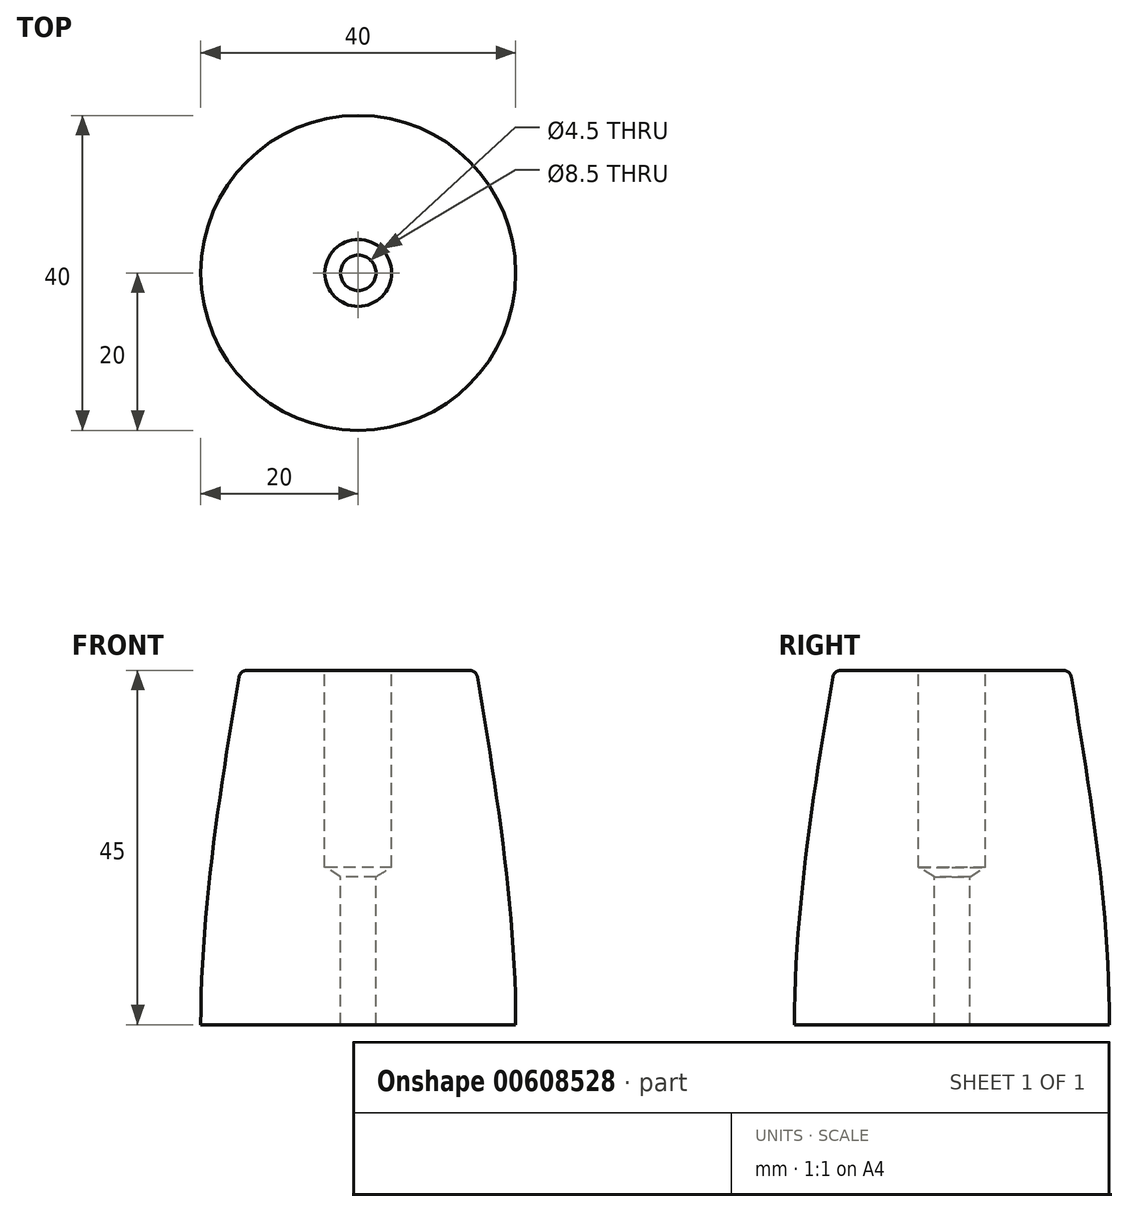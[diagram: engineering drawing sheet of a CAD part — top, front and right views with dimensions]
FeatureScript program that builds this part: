
annotation { "Feature Type Name" : "Feature", "Feature Type Description" : "" }
export const myFeature = defineFeature(function(context is Context, id is Id, definition is map)
    precondition{}
    {
        {
            var Q0;
            Q0=qCreatedBy(makeId("Top.planeOp"),FACE);
            var sketch = newSketch(context, id + "F0", { "sketchPlane" : qUnion([Q0])});
            skCircle(sketch, "E0", {"center": v(0, 0) * mm, "radius": 20 * mm});
            skSolve(sketch);
        }
        {
            var Q0;
            Q0=qCreatedBy(makeId("Top.planeOp"),FACE);
            cPlane(context, id + "F1", {"entities" : qUnion([Q0]), "cplaneType" : CPlaneType.OFFSET, "offset" : 45 * mm, "width" : 150 * mm, "height" : 150 * mm});
        }
        {
            var Q0;
            Q0=qCreatedBy(id+"F1.planeOp",FACE);
            var sketch = newSketch(context, id + "F2", { "sketchPlane" : qUnion([Q0])});
            skCircle(sketch, "E1.0", {"center": v(0, 0) * mm, "radius": 20 * mm, "construction": true});
            skCircle(sketch, "E2.0", {"center": v(0, 0) * mm, "radius": 15 * mm});
            skSolve(sketch);
        }
        {
            var Q0;
            Q0=makeQuery(id+"F0.imprint","IMPRINT",FACE,{"disambiguationData":[TD([[makeQuery(id+"F0.imprint","IMPRINT",EDGE,{"derivedFrom":sQuery(id+"F0.wireOp",EDGE,"E0")}),1.0]])]});
            var Q1;
            Q1=makeQuery(id+"F2.imprint","IMPRINT",FACE,{"disambiguationData":[TD([[makeQuery(id+"F2.imprint","IMPRINT",EDGE,{"derivedFrom":sQuery(id+"F2.wireOp",EDGE,"E2.0")}),1.0]])]});
            loft(context, id + "F3", {"startCondition" : LoftEndDerivativeType.NORMAL_TO_PROFILE, "startMagnitude" : 1, "sheetProfilesArray" : [{ "sheetProfileEntities" : qUnion([Q0]) }, { "sheetProfileEntities" : qUnion([Q1]) }]});
        }
        {
            var Q0;
            Q0=sQuery(id+"F2.wireOp",VERTEX,"E1.0.center");
            var Q1;
            Q1=makeQuery(id+"F3.opLoft","SWEPT_BODY",BODY,{"disambiguationData":[OSD([makeQuery(id+"F0.imprint","IMPRINT",FACE,{"disambiguationData":[TD([[makeQuery(id+"F0.imprint","IMPRINT",EDGE,{"derivedFrom":sQuery(id+"F0.wireOp",EDGE,"E0")}),1.0]])]}),makeQuery(id+"F2.imprint","IMPRINT",FACE,{"disambiguationData":[TD([[makeQuery(id+"F2.imprint","IMPRINT",EDGE,{"derivedFrom":sQuery(id+"F2.wireOp",EDGE,"E2.0")}),1.0]])]})])]});
            hole(context, id + "F4", {"style" : HoleStyle.SIMPLE, "endStyle" : HoleEndStyle.THROUGH, "holeDiameter" : 4.5 * mm, "majorDiameter" : 5 * mm, "isTappedThrough" : true, "tappedDepth" : 12 * mm, "tapClearance" : 3, "locations" : qUnion([Q0]), "scope" : qUnion([Q1])});
        }
        {
            var Q0;
            Q0=sQuery(id+"F2.wireOp",VERTEX,"E1.0.center");
            var Q1;
            Q1=makeQuery(id+"F3.opLoft","SWEPT_BODY",BODY,{"disambiguationData":[OSD([makeQuery(id+"F0.imprint","IMPRINT",FACE,{"disambiguationData":[TD([[makeQuery(id+"F0.imprint","IMPRINT",EDGE,{"derivedFrom":sQuery(id+"F0.wireOp",EDGE,"E0")}),1.0]])]}),makeQuery(id+"F2.imprint","IMPRINT",FACE,{"disambiguationData":[TD([[makeQuery(id+"F2.imprint","IMPRINT",EDGE,{"derivedFrom":sQuery(id+"F2.wireOp",EDGE,"E2.0")}),1.0]])]})])]});
            hole(context, id + "F5", {"style" : HoleStyle.SIMPLE, "endStyle" : HoleEndStyle.BLIND, "holeDiameter" : 8.5 * mm, "majorDiameter" : 5 * mm, "holeDepth" : 25 * mm, "isTappedThrough" : true, "tappedDepth" : 12 * mm, "tapClearance" : 3, "locations" : qUnion([Q0]), "scope" : qUnion([Q1])});
        }
        {
            var Q0;
            Q0=makeQuery(id+"F5.hole-0.boolean.opBoolean","COPY",EDGE,{"derivedFrom":makeQuery(id+"F5.hole-0.opRevolve","SWEPT_EDGE",EDGE,{"disambiguationData":[OSD([sQuery(id+"F5.hole-0.sketch.wireOp",EDGE,"core_line_2"),sQuery(id+"F5.hole-0.sketch.wireOp",EDGE,"core_line_3")])]})});
            var Q1;
            Q1=makeQuery(id+"F3.opLoft","MID_CAP_EDGE",EDGE,{"disambiguationData":[OSD([sQuery(id+"F0.wireOp",EDGE,"E0"),sQuery(id+"F2.wireOp",EDGE,"E2.0")])],"capPos":1.0});
            fillet(context, id + "F6", {"entities" : qUnion([Q0, Q1]), "radius" : 1 * mm, "tangentPropagation" : true, "allowEdgeOverflow" : false});
        }
    });
